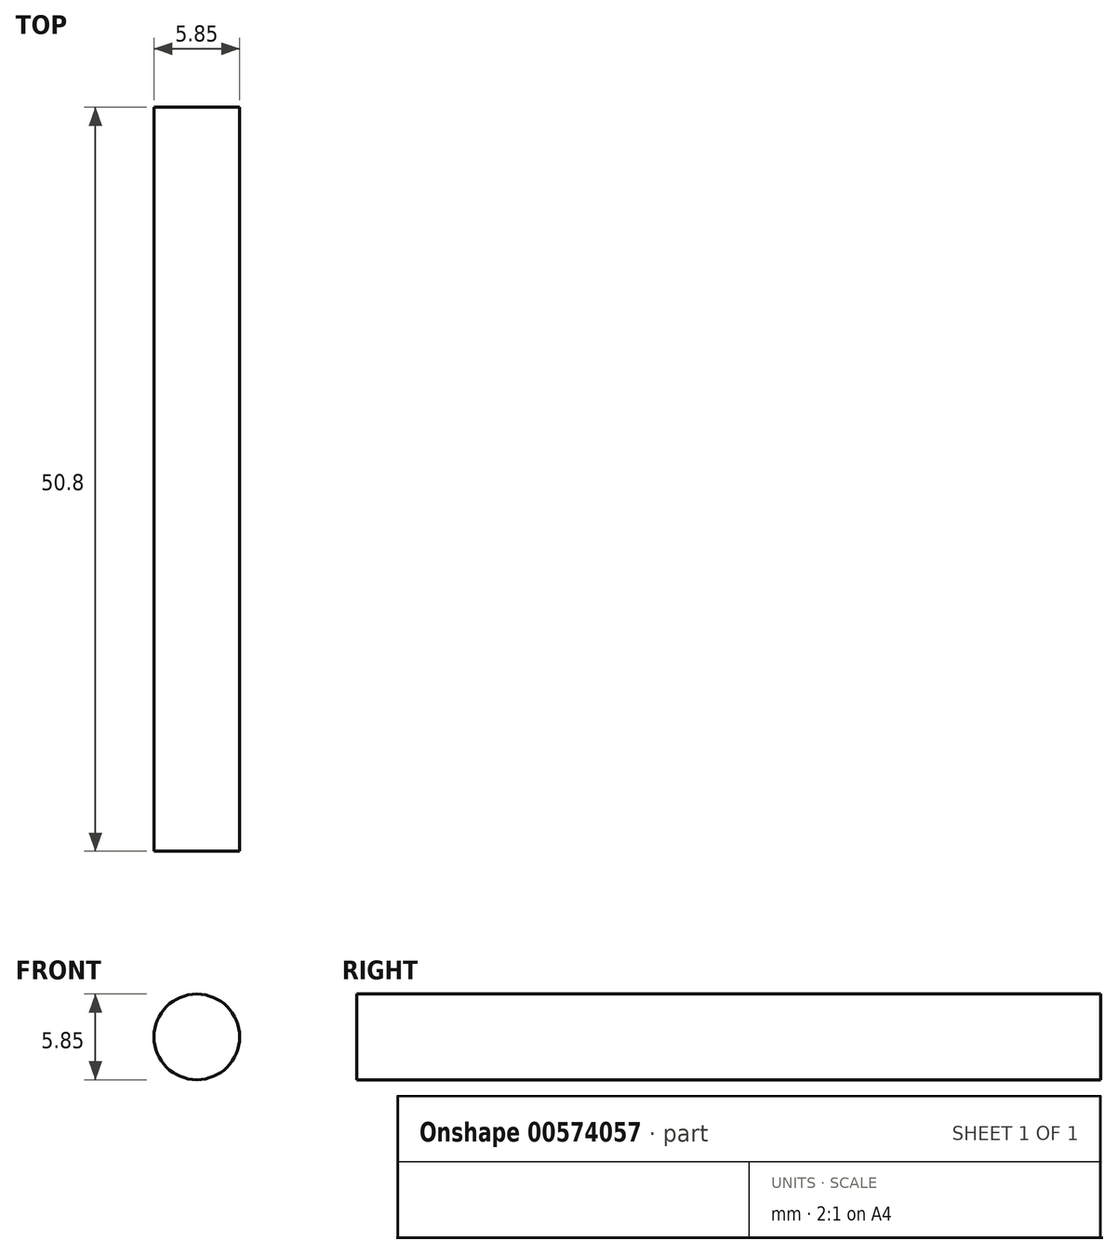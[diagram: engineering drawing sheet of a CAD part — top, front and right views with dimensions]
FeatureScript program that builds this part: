
annotation { "Feature Type Name" : "Feature", "Feature Type Description" : "" }
export const myFeature = defineFeature(function(context is Context, id is Id, definition is map)
    precondition{}
    {
        {
            var Q0;
            Q0=qCreatedBy(makeId("Front.planeOp"),FACE);
            var sketch = newSketch(context, id + "F0", { "sketchPlane" : qUnion([Q0])});
            skCircle(sketch, "E0", {"center": v(-12.38, -8.26) * mm, "radius": 2.92 * mm});
            skSolve(sketch);
        }
        {
            var Q0;
            Q0=sQuery(id+"F0.wireOp",EDGE,"E0");
            extrude(context, id + "F1", {"bodyType" : ToolBodyType.SURFACE, "surfaceEntities" : qUnion([Q0]), "depth" : 50.8 * mm, "offsetDistance" : 25.4 * mm});
        }
        {
            var Q0;
            Q0 = qSketchRegion(id + "F0", true);
            extrude(context, id + "F2", {"entities" : qUnion([Q0]), "depth" : 25.4 * mm, "offsetDistance" : 25.4 * mm});
        }
        {
            var Q0;
            Q0=makeQuery(id+"F2.opExtrude","CAP_FACE",FACE,{"disambiguationData":[OSD([sQuery(id+"F0.wireOp",EDGE,"E0")])],"isStart":false});
            extrude(context, id + "F3", {"entities" : qUnion([Q0]), "operationType" : NewBodyOperationType.ADD, "depth" : 25.4 * mm, "offsetDistance" : 25.4 * mm});
        }
    });
